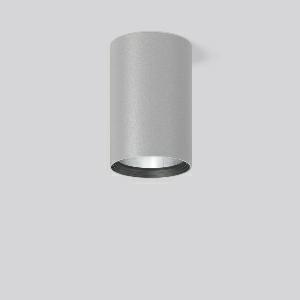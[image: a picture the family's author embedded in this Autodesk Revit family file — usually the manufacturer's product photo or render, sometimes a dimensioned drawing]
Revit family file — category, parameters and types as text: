
# Revit family: heledon_maxi_a_931224_004_1_76_06c5
name_source: partatom
category: Lighting Fixtures
units: mm (PartAtom-declared; Revit-internal decimal feet)

## family parameters
Cut with Voids When Loaded = No
Host = Face
Light Source = No
Part Type = Normal
Room Calculation Point = No
Round Connector Dimension = Use Diameter
Shared = No

## types (1)
- HELEDON maxi A (1 x LED Modul 940, 4550 lm, 4000)
    Apparent Load = 35 VA
    Approval mark = CE
    CIE Flux Codes = 100 100 100 100 100
    Color Rendering = 92
    Color Temperature = 4000
    Default Elevation = 1800 mm
    Description = Series: HELEDON maxi
Cylindrical surface-mounted downlight. Housing: die-cast aluminium, powder-coated. Internal ceiling frame polycarbonate with bayonet mounting. Black plastic ring and recessed LED to prevent glare from the side. Optical assembly with reflector made of MIRO-Silver with 98% total light reflection for outstanding efficiency - can be changed without tools. Best colour rendering index Ra>90. Suitable for Ceiling mounting. Easy installation with a separate ceiling frame with bayonet mounting and plug connection. Driver integrated. Connected via plug-in connector. High quality converter without flickering and stroboscopic effect. The following accessories can be mounted without use of tools: interchangeable lenses, decorative glasses, honeycomb louvre, clear and frosted diffusers, white interchangeable plastic ring. 
Colour: silver
Diameter: 123 mm
Height: 183 mm
Lamp: LED
Socket: without socket
Colour temperature: 4000K
Colour rendering index (CRI): 92
System power: 35 W
Rated luminous flux: 4550 lm
Luminous efficiency: 130 lm/W
Control gear: Converter, dimmable, DALI
Protection class: I
Type of protection: IP 20
    Height = 183 mm
    Lamp = 1 x LED Modul 940
    Lamp Light Flux = 4550 lm
    Lamp count = 1
    Length = 123 mm
    Lifetime = 50000 h
    Luminous efficacy = 130 lm/W
    Manufacturer = RZB
    ModVariant = No
    Model = 931224.004.1.76
    Mounting Place = Ceiling
    Mounting Type = Surface mounted
    Number of Poles = 1
    OnlyDefault = Yes
    Power Factor = 1
    Product Name = HELEDON maxi A
    Product group = Surface mounted downlights
    ProductGroupID = 302
    Protection Class = Protection class I
    Protection Degree = IP 20
    RLX_Detail_Level = 1
    RLX_Emergency_Light_Flux = 0 lm
    RLX_Emergency_Type = 0
    RLX_Emergency_Type_DB = No
    RlxData = <blob elided: 100969 chars, md5=da4922e1>
    Socket = socket
    Standby Power = 0 W
    System Light Flux = 4550 lm
    System Power = 35 W
    Type Comments = Product without accessories
    Type Image = 931192.004.jpg
    URL = http://relux.com
    VarID = ---
    Voltage = 230 V
    Voltage Range = 220-240 V
    Weight = 0.00 kg
    Width = 0 mm  [stored 0 ft]

note: [stored X ft] marks values corroborated as IEEE doubles in the binary element streams (Revit-internal decimal feet)

## geometry (parser evidence)
native form markers: Blend x4, Sweep x10
no freeform markers — native parametric forms only
